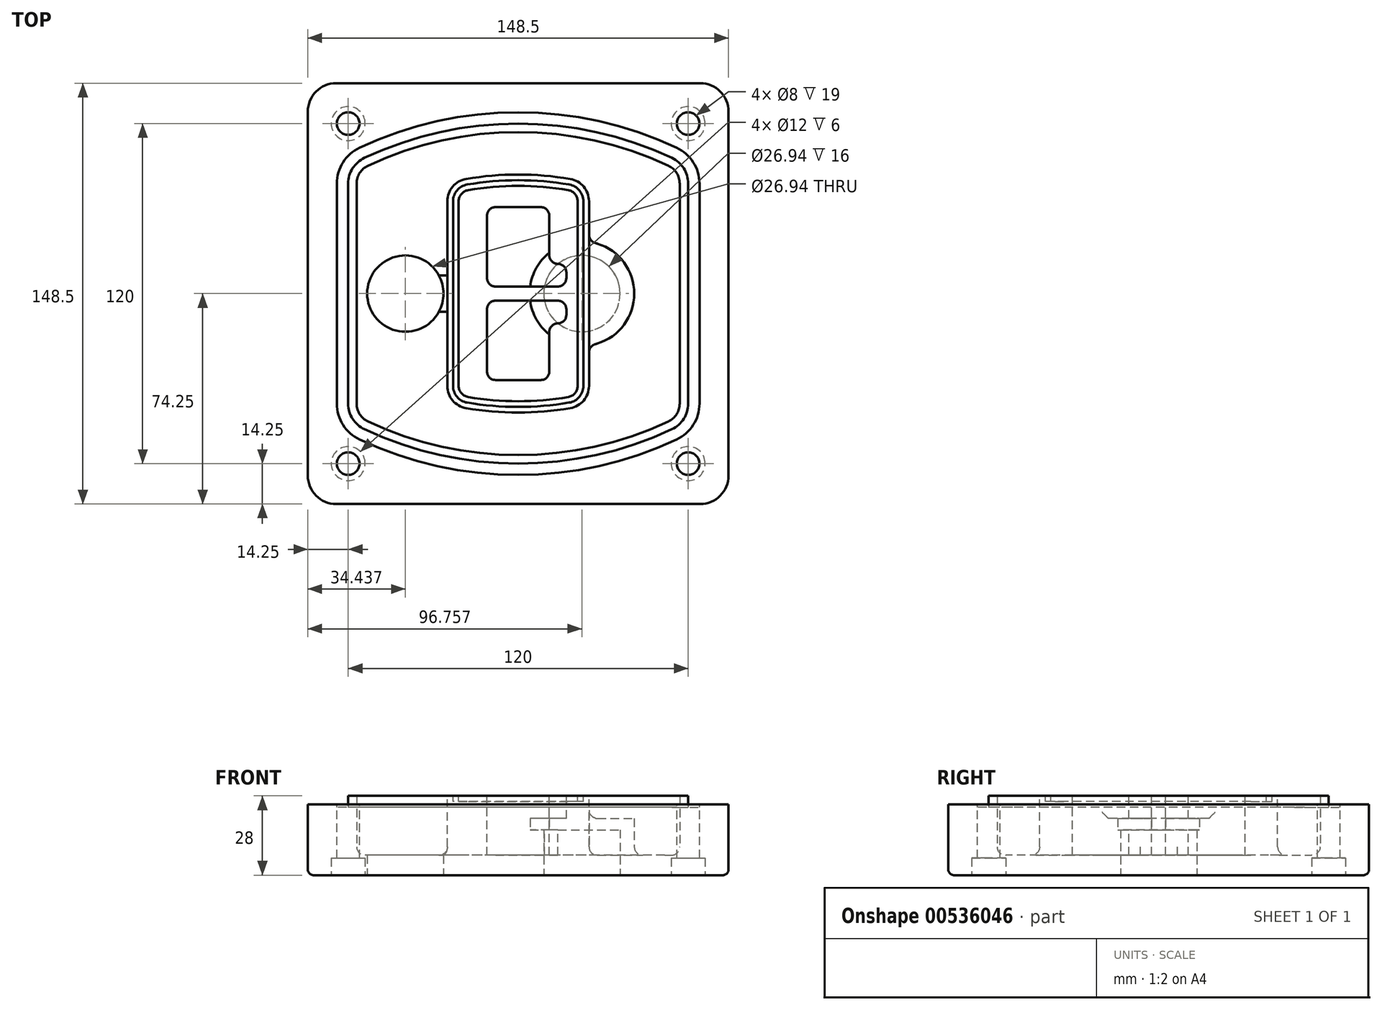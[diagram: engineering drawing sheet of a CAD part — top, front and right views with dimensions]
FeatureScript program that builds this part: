
annotation { "Feature Type Name" : "Feature", "Feature Type Description" : "" }
export const myFeature = defineFeature(function(context is Context, id is Id, definition is map)
    precondition{}
    {
        {
            var Q0;
            Q0=qCreatedBy(makeId("Top.planeOp"),FACE);
            var sketch = newSketch(context, id + "F0", { "sketchPlane" : qUnion([Q0])});
            skPoint(sketch, "E0.rect.middle", {"position": v(0, 0) * mm});
            skLineSegment(sketch, "E1.bottom", {"start": v(-64.25, -74.25) * mm, "end": v(64.25, -74.25) * mm});
            skLineSegment(sketch, "E1.top", {"start": v(-64.25, 74.25) * mm, "end": v(64.25, 74.25) * mm});
            skLineSegment(sketch, "E1.left", {"start": v(-74.25, -64.25) * mm, "end": v(-74.25, 64.25) * mm});
            skLineSegment(sketch, "E1.right", {"start": v(74.25, -64.25) * mm, "end": v(74.25, 64.25) * mm});
            skLineSegment(sketch, "E2", {"start": v(-74.25, 74.25) * mm, "end": v(74.25, -74.25) * mm, "construction": true});
            skLineSegment(sketch, "E3", {"start": v(74.25, 74.25) * mm, "end": v(-74.25, -74.25) * mm, "construction": true});
            skCircle(sketch, "E4", {"center": v(-60, 60) * mm, "radius": 4 * mm});
            skCircle(sketch, "E5", {"center": v(60, 60) * mm, "radius": 4 * mm});
            skCircle(sketch, "E6", {"center": v(60, -60) * mm, "radius": 4 * mm});
            skCircle(sketch, "E7", {"center": v(-60, -60) * mm, "radius": 4 * mm});
            skLineSegment(sketch, "E8", {"start": v(-60, 60) * mm, "end": v(60, 60) * mm, "construction": true});
            skLineSegment(sketch, "E9", {"start": v(60, 60) * mm, "end": v(60, -60) * mm, "construction": true});
            skLineSegment(sketch, "E10", {"start": v(60, -60) * mm, "end": v(-60, -60) * mm, "construction": true});
            skLineSegment(sketch, "E11", {"start": v(-60, -60) * mm, "end": v(-60, 60) * mm, "construction": true});
            skLineSegment(sketch, "E12", {"start": v(-60, 38.83) * mm, "end": v(-60, -38.83) * mm});
            skLineSegment(sketch, "E13", {"start": v(60, 38.83) * mm, "end": v(60, -38.83) * mm});
            skArc(sketch, "E14", {"start": v(54.26, 47.88) * mm, "mid": v(0, 60) * mm, "end": v(-54.26, 47.88) * mm});
            skArc(sketch, "E15", {"start": v(-54.26, -47.88) * mm, "mid": v(0, -60) * mm, "end": v(54.26, -47.88) * mm});
            skLineSegment(sketch, "E16", {"start": v(-60, 0) * mm, "end": v(60, 0) * mm, "construction": true});
            skPoint(sketch, "E17.visualSharp", {"position": v(-60, -45) * mm});
            skArc(sketch, "E17.filletArc", {"start": v(-60, -38.83) * mm, "mid": v(-58.44, -44.2) * mm, "end": v(-54.26, -47.88) * mm});
            skPoint(sketch, "E18.visualSharp", {"position": v(-60, 45) * mm});
            skArc(sketch, "E18.filletArc", {"start": v(-54.26, 47.88) * mm, "mid": v(-58.44, 44.2) * mm, "end": v(-60, 38.83) * mm});
            skPoint(sketch, "E19.visualSharp", {"position": v(60, 45) * mm});
            skArc(sketch, "E19.filletArc", {"start": v(60, 38.83) * mm, "mid": v(58.44, 44.2) * mm, "end": v(54.26, 47.88) * mm});
            skPoint(sketch, "E20.visualSharp", {"position": v(60, -45) * mm});
            skArc(sketch, "E20.filletArc", {"start": v(54.26, -47.88) * mm, "mid": v(58.44, -44.2) * mm, "end": v(60, -38.83) * mm});
            skPoint(sketch, "E21.visualSharp", {"position": v(-74.25, 74.25) * mm});
            skArc(sketch, "E21.filletArc", {"start": v(-64.25, 74.25) * mm, "mid": v(-71.32, 71.32) * mm, "end": v(-74.25, 64.25) * mm});
            skPoint(sketch, "E22.visualSharp", {"position": v(74.25, 74.25) * mm});
            skArc(sketch, "E22.filletArc", {"start": v(74.25, 64.25) * mm, "mid": v(71.32, 71.32) * mm, "end": v(64.25, 74.25) * mm});
            skPoint(sketch, "E23.visualSharp", {"position": v(74.25, -74.25) * mm});
            skArc(sketch, "E23.filletArc", {"start": v(64.25, -74.25) * mm, "mid": v(71.32, -71.32) * mm, "end": v(74.25, -64.25) * mm});
            skPoint(sketch, "E24.visualSharp", {"position": v(-74.25, -74.25) * mm});
            skArc(sketch, "E24.filletArc", {"start": v(-74.25, -64.25) * mm, "mid": v(-71.32, -71.32) * mm, "end": v(-64.25, -74.25) * mm});
            skArc(sketch, "E25.0", {"start": v(57, 38.83) * mm, "mid": v(55.9, 42.58) * mm, "end": v(52.98, 45.17) * mm});
            skLineSegment(sketch, "E25.1", {"start": v(57, 38.83) * mm, "end": v(57, -38.83) * mm});
            skArc(sketch, "E25.2", {"start": v(52.98, -45.17) * mm, "mid": v(55.9, -42.58) * mm, "end": v(57, -38.83) * mm});
            skArc(sketch, "E25.3", {"start": v(-52.98, -45.17) * mm, "mid": v(0, -57) * mm, "end": v(52.98, -45.17) * mm});
            skArc(sketch, "E25.4", {"start": v(-57, -38.83) * mm, "mid": v(-55.9, -42.58) * mm, "end": v(-52.98, -45.17) * mm});
            skArc(sketch, "E25.5", {"start": v(52.98, 45.17) * mm, "mid": v(0, 57) * mm, "end": v(-52.98, 45.17) * mm});
            skLineSegment(sketch, "E25.6", {"start": v(-57, 38.83) * mm, "end": v(-57, -38.83) * mm});
            skArc(sketch, "E25.7", {"start": v(-52.98, 45.17) * mm, "mid": v(-55.9, 42.58) * mm, "end": v(-57, 38.83) * mm});
            skArc(sketch, "E26.0", {"start": v(-55.96, 51.5) * mm, "mid": v(-61.82, 46.33) * mm, "end": v(-64, 38.83) * mm});
            skArc(sketch, "E26.1", {"start": v(55.96, 51.5) * mm, "mid": v(0, 64) * mm, "end": v(-55.96, 51.5) * mm});
            skArc(sketch, "E26.2", {"start": v(64, 38.83) * mm, "mid": v(61.82, 46.33) * mm, "end": v(55.96, 51.5) * mm});
            skLineSegment(sketch, "E26.3", {"start": v(64, 38.83) * mm, "end": v(64, -38.83) * mm});
            skArc(sketch, "E26.4", {"start": v(55.96, -51.5) * mm, "mid": v(61.82, -46.33) * mm, "end": v(64, -38.83) * mm});
            skLineSegment(sketch, "E26.5", {"start": v(-64, 38.83) * mm, "end": v(-64, -38.83) * mm});
            skArc(sketch, "E26.6", {"start": v(-55.96, -51.5) * mm, "mid": v(0, -64) * mm, "end": v(55.96, -51.5) * mm});
            skArc(sketch, "E26.7", {"start": v(-64, -38.83) * mm, "mid": v(-61.82, -46.33) * mm, "end": v(-55.96, -51.5) * mm});
            skSolve(sketch);
        }
        {
            var Q0;
            Q0=makeQuery(id+"F0.imprint","IMPRINT",FACE,{"disambiguationData":[TD([[makeQuery(id+"F0.imprint","IMPRINT",EDGE,{"derivedFrom":sQuery(id+"F0.wireOp",EDGE,"E1.bottom")}),1.0]])]});
            var Q1;
            Q1=makeQuery(id+"F0.imprint","IMPRINT",FACE,{"disambiguationData":[TD([[makeQuery(id+"F0.imprint","IMPRINT",EDGE,{"derivedFrom":sQuery(id+"F0.wireOp",EDGE,"E12")}),1.0]])]});
            var Q2;
            Q2=makeQuery(id+"F0.imprint","IMPRINT",FACE,{"disambiguationData":[TD([[makeQuery(id+"F0.imprint","IMPRINT",EDGE,{"derivedFrom":sQuery(id+"F0.wireOp",EDGE,"E25.0")}),1.0]])]});
            var Q3;
            Q3=makeQuery(id+"F0.imprint","IMPRINT",FACE,{"disambiguationData":[TD([[makeQuery(id+"F0.imprint","IMPRINT",EDGE,{"derivedFrom":sQuery(id+"F0.wireOp",EDGE,"E12")}),-1.0]])]});
            extrude(context, id + "F1", {"entities" : qUnion([Q0, Q1, Q2, Q3]), "oppositeDirection" : true, "depth" : 25 * mm, "offsetDistance" : 25 * mm});
        }
        {
            var Q0;
            Q0=makeQuery(id+"F0.imprint","IMPRINT",FACE,{"disambiguationData":[TD([[makeQuery(id+"F0.imprint","IMPRINT",EDGE,{"derivedFrom":sQuery(id+"F0.wireOp",EDGE,"E12")}),1.0]])]});
            extrude(context, id + "F2", {"entities" : qUnion([Q0]), "operationType" : NewBodyOperationType.ADD, "depth" : 3 * mm, "offsetDistance" : 25 * mm});
        }
        {
            var Q0;
            Q0=makeQuery(id+"F0.imprint","IMPRINT",FACE,{"disambiguationData":[TD([[makeQuery(id+"F0.imprint","IMPRINT",EDGE,{"derivedFrom":sQuery(id+"F0.wireOp",EDGE,"E12")}),-1.0]])]});
            extrude(context, id + "F3", {"entities" : qUnion([Q0]), "operationType" : NewBodyOperationType.REMOVE, "oppositeDirection" : true, "depth" : 1 * mm});
        }
        {
            var Q0;
            Q0=makeQuery(id+"F0.imprint","IMPRINT",FACE,{"disambiguationData":[TD([[makeQuery(id+"F0.imprint","IMPRINT",EDGE,{"derivedFrom":sQuery(id+"F0.wireOp",EDGE,"E25.0")}),1.0]])]});
            extrude(context, id + "F4", {"entities" : qUnion([Q0]), "operationType" : NewBodyOperationType.REMOVE, "oppositeDirection" : true, "depth" : 18 * mm});
        }
        {
            var Q0;
            Q0=makeQuery(id+"F2.opExtrude","CAP_FACE",FACE,{"disambiguationData":[OSD([sQuery(id+"F0.wireOp",EDGE,"E12"),sQuery(id+"F0.wireOp",EDGE,"E13"),sQuery(id+"F0.wireOp",EDGE,"E14"),sQuery(id+"F0.wireOp",EDGE,"E15"),sQuery(id+"F0.wireOp",EDGE,"E17.filletArc"),sQuery(id+"F0.wireOp",EDGE,"E18.filletArc"),sQuery(id+"F0.wireOp",EDGE,"E19.filletArc"),sQuery(id+"F0.wireOp",EDGE,"E20.filletArc"),sQuery(id+"F0.wireOp",EDGE,"E25.0"),sQuery(id+"F0.wireOp",EDGE,"E25.1"),sQuery(id+"F0.wireOp",EDGE,"E25.2"),sQuery(id+"F0.wireOp",EDGE,"E25.3"),sQuery(id+"F0.wireOp",EDGE,"E25.4"),sQuery(id+"F0.wireOp",EDGE,"E25.5"),sQuery(id+"F0.wireOp",EDGE,"E25.6"),sQuery(id+"F0.wireOp",EDGE,"E25.7")])],"isStart":false});
            var sketch = newSketch(context, id + "F5", { "sketchPlane" : qUnion([Q0])});
            skArc(sketch, "E27.0", {"start": v(-18.34, -40.45) * mm, "mid": v(0, -42) * mm, "end": v(18.34, -40.45) * mm});
            skArc(sketch, "E28.0", {"start": v(18.34, 40.45) * mm, "mid": v(0, 42) * mm, "end": v(-18.34, 40.45) * mm});
            skLineSegment(sketch, "E29", {"start": v(-25, 32.57) * mm, "end": v(-25, -32.57) * mm});
            skLineSegment(sketch, "E30", {"start": v(25, 32.57) * mm, "end": v(25, -32.57) * mm});
            skLineSegment(sketch, "E31", {"start": v(-25, 39.1) * mm, "end": v(25, 39.1) * mm, "construction": true});
            skLineSegment(sketch, "E32", {"start": v(-25, -39.1) * mm, "end": v(25, -39.1) * mm, "construction": true});
            skPoint(sketch, "E33.visualSharp", {"position": v(-25, 39.1) * mm});
            skArc(sketch, "E33.filletArc", {"start": v(-18.34, 40.45) * mm, "mid": v(-23.11, 37.73) * mm, "end": v(-25, 32.57) * mm});
            skPoint(sketch, "E34.visualSharp", {"position": v(25, 39.1) * mm});
            skArc(sketch, "E34.filletArc", {"start": v(25, 32.57) * mm, "mid": v(23.11, 37.73) * mm, "end": v(18.34, 40.45) * mm});
            skPoint(sketch, "E35.visualSharp", {"position": v(25, -39.1) * mm});
            skArc(sketch, "E35.filletArc", {"start": v(18.34, -40.45) * mm, "mid": v(23.11, -37.73) * mm, "end": v(25, -32.57) * mm});
            skPoint(sketch, "E36.visualSharp", {"position": v(-25, -39.1) * mm});
            skArc(sketch, "E36.filletArc", {"start": v(-25, -32.57) * mm, "mid": v(-23.11, -37.73) * mm, "end": v(-18.34, -40.45) * mm});
            skArc(sketch, "E37.0", {"start": v(52.98, 45.17) * mm, "mid": v(0, 57) * mm, "end": v(-52.98, 45.17) * mm});
            skArc(sketch, "E37.1", {"start": v(-52.98, 45.17) * mm, "mid": v(-55.9, 42.58) * mm, "end": v(-57, 38.83) * mm});
            skLineSegment(sketch, "E37.2", {"start": v(-57, 38.83) * mm, "end": v(-57, -38.83) * mm});
            skArc(sketch, "E37.3", {"start": v(-57, -38.83) * mm, "mid": v(-55.9, -42.58) * mm, "end": v(-52.98, -45.17) * mm});
            skArc(sketch, "E37.4", {"start": v(-52.98, -45.17) * mm, "mid": v(0, -57) * mm, "end": v(52.98, -45.17) * mm});
            skArc(sketch, "E37.5", {"start": v(52.98, -45.17) * mm, "mid": v(55.9, -42.58) * mm, "end": v(57, -38.83) * mm});
            skLineSegment(sketch, "E37.6", {"start": v(57, 38.83) * mm, "end": v(57, -38.83) * mm});
            skArc(sketch, "E37.7", {"start": v(57, 38.83) * mm, "mid": v(55.9, 42.58) * mm, "end": v(52.98, 45.17) * mm});
            skLineSegment(sketch, "E38.0", {"start": v(23, 32.57) * mm, "end": v(23, -32.57) * mm});
            skArc(sketch, "E38.1", {"start": v(18, -38.48) * mm, "mid": v(21.58, -36.44) * mm, "end": v(23, -32.57) * mm});
            skArc(sketch, "E38.2", {"start": v(-18, -38.48) * mm, "mid": v(0, -40) * mm, "end": v(18, -38.48) * mm});
            skArc(sketch, "E38.3", {"start": v(-23, -32.57) * mm, "mid": v(-21.58, -36.44) * mm, "end": v(-18, -38.48) * mm});
            skLineSegment(sketch, "E38.4", {"start": v(-23, 32.57) * mm, "end": v(-23, -32.57) * mm});
            skArc(sketch, "E38.5", {"start": v(23, 32.57) * mm, "mid": v(21.58, 36.44) * mm, "end": v(18, 38.48) * mm});
            skArc(sketch, "E38.6", {"start": v(-18, 38.48) * mm, "mid": v(-21.58, 36.44) * mm, "end": v(-23, 32.57) * mm});
            skArc(sketch, "E38.7", {"start": v(18, 38.48) * mm, "mid": v(0, 40) * mm, "end": v(-18, 38.48) * mm});
            skArc(sketch, "E39.0", {"start": v(21, 32.57) * mm, "mid": v(20.06, 35.15) * mm, "end": v(17.67, 36.5) * mm});
            skLineSegment(sketch, "E39.1", {"start": v(21, 32.57) * mm, "end": v(21, -32.57) * mm});
            skArc(sketch, "E39.2", {"start": v(17.67, -36.5) * mm, "mid": v(20.06, -35.15) * mm, "end": v(21, -32.57) * mm});
            skArc(sketch, "E39.3", {"start": v(-17.67, -36.5) * mm, "mid": v(0, -38) * mm, "end": v(17.67, -36.5) * mm});
            skArc(sketch, "E39.4", {"start": v(-21, -32.57) * mm, "mid": v(-20.06, -35.15) * mm, "end": v(-17.67, -36.5) * mm});
            skArc(sketch, "E39.5", {"start": v(17.67, 36.5) * mm, "mid": v(0, 38) * mm, "end": v(-17.67, 36.5) * mm});
            skLineSegment(sketch, "E39.6", {"start": v(-21, 32.57) * mm, "end": v(-21, -32.57) * mm});
            skArc(sketch, "E39.7", {"start": v(-17.67, 36.5) * mm, "mid": v(-20.06, 35.15) * mm, "end": v(-21, 32.57) * mm});
            skLineSegment(sketch, "E40", {"start": v(-25, 0) * mm, "end": v(25, 0) * mm, "construction": true});
            skLineSegment(sketch, "E41", {"start": v(-11, 5.5) * mm, "end": v(-11, 27.5) * mm});
            skLineSegment(sketch, "E42", {"start": v(-8, 30.5) * mm, "end": v(8, 30.5) * mm});
            skLineSegment(sketch, "E43", {"start": v(11, 27.5) * mm, "end": v(11, 13.5) * mm});
            skLineSegment(sketch, "E44", {"start": v(14, 10.5) * mm, "end": v(14, 10.5) * mm});
            skLineSegment(sketch, "E45", {"start": v(17, 7.5) * mm, "end": v(17, 5.5) * mm});
            skLineSegment(sketch, "E46", {"start": v(14, 2.5) * mm, "end": v(-8, 2.5) * mm});
            skPoint(sketch, "E47.visualSharp", {"position": v(-11, 30.5) * mm});
            skArc(sketch, "E47.filletArc", {"start": v(-8, 30.5) * mm, "mid": v(-10.12, 29.62) * mm, "end": v(-11, 27.5) * mm});
            skPoint(sketch, "E48.visualSharp", {"position": v(11, 30.5) * mm});
            skArc(sketch, "E48.filletArc", {"start": v(11, 27.5) * mm, "mid": v(10.12, 29.62) * mm, "end": v(8, 30.5) * mm});
            skPoint(sketch, "E49.visualSharp", {"position": v(11, 10.5) * mm});
            skArc(sketch, "E49.filletArc", {"start": v(11, 13.5) * mm, "mid": v(11.88, 11.38) * mm, "end": v(14, 10.5) * mm});
            skPoint(sketch, "E50.visualSharp", {"position": v(17, 10.5) * mm});
            skArc(sketch, "E50.filletArc", {"start": v(17, 7.5) * mm, "mid": v(16.12, 9.62) * mm, "end": v(14, 10.5) * mm});
            skPoint(sketch, "E51.visualSharp", {"position": v(17, 2.5) * mm});
            skArc(sketch, "E51.filletArc", {"start": v(14, 2.5) * mm, "mid": v(16.12, 3.38) * mm, "end": v(17, 5.5) * mm});
            skPoint(sketch, "E52.visualSharp", {"position": v(-11, 2.5) * mm});
            skArc(sketch, "E52.filletArc", {"start": v(-11, 5.5) * mm, "mid": v(-10.12, 3.38) * mm, "end": v(-8, 2.5) * mm});
            skLineSegment(sketch, "E53.0.MirrorCS", {"start": v(14, -2.5) * mm, "end": v(-8, -2.5) * mm});
            skArc(sketch, "E54.0.MirrorCS", {"start": v(-11, -5.5) * mm, "mid": v(-10.12, -3.38) * mm, "end": v(-8, -2.5) * mm});
            skLineSegment(sketch, "E55.0.MirrorCS", {"start": v(-11, -5.5) * mm, "end": v(-11, -27.5) * mm});
            skArc(sketch, "E56.0.MirrorCS", {"start": v(-8, -30.5) * mm, "mid": v(-10.12, -29.62) * mm, "end": v(-11, -27.5) * mm});
            skLineSegment(sketch, "E57.0.MirrorCS", {"start": v(-8, -30.5) * mm, "end": v(8, -30.5) * mm});
            skArc(sketch, "E58.0.MirrorCS", {"start": v(11, -27.5) * mm, "mid": v(10.12, -29.62) * mm, "end": v(8, -30.5) * mm});
            skLineSegment(sketch, "E59.0.MirrorCS", {"start": v(11, -27.5) * mm, "end": v(11, -13.5) * mm});
            skArc(sketch, "E60.0.MirrorCS", {"start": v(11, -13.5) * mm, "mid": v(11.88, -11.38) * mm, "end": v(14, -10.5) * mm});
            skArc(sketch, "E61.0.MirrorCS", {"start": v(17, -7.5) * mm, "mid": v(16.12, -9.62) * mm, "end": v(14, -10.5) * mm});
            skLineSegment(sketch, "E62.0.MirrorCS", {"start": v(17, -7.5) * mm, "end": v(17, -5.5) * mm});
            skArc(sketch, "E63.0.MirrorCS", {"start": v(14, -2.5) * mm, "mid": v(16.12, -3.38) * mm, "end": v(17, -5.5) * mm});
            skSolve(sketch);
        }
        {
            var Q0;
            Q0=makeQuery(id+"F5.imprint","IMPRINT",FACE,{"disambiguationData":[TD([[makeQuery(id+"F5.imprint","IMPRINT",EDGE,{"derivedFrom":sQuery(id+"F5.wireOp",EDGE,"E27.0")}),1.0]])]});
            var Q1;
            Q1=makeQuery(id+"F5.imprint","IMPRINT",FACE,{"disambiguationData":[TD([[makeQuery(id+"F5.imprint","IMPRINT",EDGE,{"derivedFrom":sQuery(id+"F5.wireOp",EDGE,"E38.0")}),-1.0]])]});
            var Q2;
            Q2=makeQuery(id+"F5.imprint","IMPRINT",FACE,{"disambiguationData":[TD([[makeQuery(id+"F5.imprint","IMPRINT",EDGE,{"derivedFrom":sQuery(id+"F5.wireOp",EDGE,"E39.0")}),1.0]])]});
            extrude(context, id + "F6", {"entities" : qUnion([Q0, Q1, Q2]), "operationType" : NewBodyOperationType.ADD, "endBound" : BoundingType.UP_TO_NEXT, "oppositeDirection" : true, "depth" : 25 * mm});
        }
        {
            var Q0;
            Q0=makeQuery(id+"F5.imprint","IMPRINT",FACE,{"disambiguationData":[TD([[makeQuery(id+"F5.imprint","IMPRINT",EDGE,{"derivedFrom":sQuery(id+"F5.wireOp",EDGE,"E38.0")}),-1.0]])]});
            extrude(context, id + "F7", {"entities" : qUnion([Q0]), "operationType" : NewBodyOperationType.REMOVE, "oppositeDirection" : true, "depth" : 2 * mm});
        }
        {
            var Q0;
            Q0=makeQuery(id+"F1.opExtrude","CAP_FACE",FACE,{"disambiguationData":[OSD([sQuery(id+"F0.wireOp",EDGE,"E1.bottom"),sQuery(id+"F0.wireOp",EDGE,"E1.top"),sQuery(id+"F0.wireOp",EDGE,"E1.left"),sQuery(id+"F0.wireOp",EDGE,"E1.right"),sQuery(id+"F0.wireOp",EDGE,"E4"),sQuery(id+"F0.wireOp",EDGE,"E5"),sQuery(id+"F0.wireOp",EDGE,"E6"),sQuery(id+"F0.wireOp",EDGE,"E7"),sQuery(id+"F0.wireOp",EDGE,"E21.filletArc"),sQuery(id+"F0.wireOp",EDGE,"E22.filletArc"),sQuery(id+"F0.wireOp",EDGE,"E23.filletArc"),sQuery(id+"F0.wireOp",EDGE,"E24.filletArc")])],"isStart":false});
            var sketch = newSketch(context, id + "F8", { "sketchPlane" : qUnion([Q0])});
            skCircle(sketch, "E64", {"center": v(22.5, 0) * mm, "radius": 13.47 * mm});
            skCircle(sketch, "E65", {"center": v(-39.81, 0) * mm, "radius": 13.47 * mm});
            skLineSegment(sketch, "E66", {"start": v(74.25, 0) * mm, "end": v(-74.25, 0) * mm});
            skCircle(sketch, "E67", {"center": v(22.5, 0) * mm, "radius": 18.47 * mm});
            skCircle(sketch, "E68", {"center": v(60, -60) * mm, "radius": 6 * mm});
            skCircle(sketch, "E69", {"center": v(-60, -60) * mm, "radius": 6 * mm});
            skCircle(sketch, "E70", {"center": v(-60, 60) * mm, "radius": 6 * mm});
            skCircle(sketch, "E71", {"center": v(60, 60) * mm, "radius": 6 * mm});
            skSolve(sketch);
        }
        {
            var Q0;
            {var subQ1=sQuery(id+"F8.wireOp",EDGE,"E66");var subQ4=sQuery(id+"F8.wireOp",EDGE,"E64");var subQ6=makeQuery(id+"F8.imprint","INTERSECT",VERTEX,{"disambiguationData":[OD(0.0)],"derivedFrom":[subQ4,subQ1]});Q0=makeQuery(id+"F8.imprint","IMPRINT",FACE,{"disambiguationData":[TD([[makeQuery(id+"F8.imprint","IMPRINT",EDGE,{"disambiguationData":[TD([[subQ6,-1.0]])],"derivedFrom":subQ4}),-1.0]])]});}
            var Q1;
            {var subQ0=sQuery(id+"F8.wireOp",EDGE,"E66");var subQ1=sQuery(id+"F8.wireOp",EDGE,"E64");var subQ3=makeQuery(id+"F8.imprint","INTERSECT",VERTEX,{"disambiguationData":[OD(0.0)],"derivedFrom":[subQ1,subQ0]});Q1=makeQuery(id+"F8.imprint","IMPRINT",FACE,{"disambiguationData":[TD([[makeQuery(id+"F8.imprint","IMPRINT",EDGE,{"disambiguationData":[TD([[subQ3,-1.0]])],"derivedFrom":subQ1}),1.0]])]});}
            var Q2;
            {var subQ0=sQuery(id+"F8.wireOp",EDGE,"E66");var subQ1=sQuery(id+"F8.wireOp",EDGE,"E64");var subQ3=makeQuery(id+"F8.imprint","INTERSECT",VERTEX,{"disambiguationData":[OD(0.0)],"derivedFrom":[subQ1,subQ0]});Q2=makeQuery(id+"F8.imprint","IMPRINT",FACE,{"disambiguationData":[TD([[makeQuery(id+"F8.imprint","IMPRINT",EDGE,{"disambiguationData":[TD([[subQ3,1.0]])],"derivedFrom":subQ1}),1.0]])]});}
            var Q3;
            {var subQ1=sQuery(id+"F8.wireOp",EDGE,"E66");var subQ4=sQuery(id+"F8.wireOp",EDGE,"E64");var subQ6=makeQuery(id+"F8.imprint","INTERSECT",VERTEX,{"disambiguationData":[OD(0.0)],"derivedFrom":[subQ4,subQ1]});Q3=makeQuery(id+"F8.imprint","IMPRINT",FACE,{"disambiguationData":[TD([[makeQuery(id+"F8.imprint","IMPRINT",EDGE,{"disambiguationData":[TD([[subQ6,1.0]])],"derivedFrom":subQ4}),-1.0]])]});}
            extrude(context, id + "F9", {"entities" : qUnion([Q0, Q1, Q2, Q3]), "operationType" : NewBodyOperationType.ADD, "oppositeDirection" : true, "depth" : 20 * mm});
        }
        {
            var Q0;
            {var subQ0=sQuery(id+"F8.wireOp",EDGE,"E66");var subQ1=sQuery(id+"F8.wireOp",EDGE,"E64");var subQ3=makeQuery(id+"F8.imprint","INTERSECT",VERTEX,{"disambiguationData":[OD(0.0)],"derivedFrom":[subQ1,subQ0]});Q0=makeQuery(id+"F8.imprint","IMPRINT",FACE,{"disambiguationData":[TD([[makeQuery(id+"F8.imprint","IMPRINT",EDGE,{"disambiguationData":[TD([[subQ3,-1.0]])],"derivedFrom":subQ1}),1.0]])]});}
            var Q1;
            {var subQ0=sQuery(id+"F8.wireOp",EDGE,"E66");var subQ1=sQuery(id+"F8.wireOp",EDGE,"E64");var subQ3=makeQuery(id+"F8.imprint","INTERSECT",VERTEX,{"disambiguationData":[OD(0.0)],"derivedFrom":[subQ1,subQ0]});Q1=makeQuery(id+"F8.imprint","IMPRINT",FACE,{"disambiguationData":[TD([[makeQuery(id+"F8.imprint","IMPRINT",EDGE,{"disambiguationData":[TD([[subQ3,1.0]])],"derivedFrom":subQ1}),1.0]])]});}
            extrude(context, id + "F10", {"entities" : qUnion([Q0, Q1]), "operationType" : NewBodyOperationType.REMOVE, "oppositeDirection" : true, "depth" : 16 * mm});
        }
        {
            var Q0;
            {var subQ0=sQuery(id+"F8.wireOp",EDGE,"E66");var subQ1=sQuery(id+"F8.wireOp",EDGE,"E65");var subQ3=makeQuery(id+"F8.imprint","INTERSECT",VERTEX,{"disambiguationData":[OD(0.0)],"derivedFrom":[subQ1,subQ0]});Q0=makeQuery(id+"F8.imprint","IMPRINT",FACE,{"disambiguationData":[TD([[makeQuery(id+"F8.imprint","IMPRINT",EDGE,{"disambiguationData":[TD([[subQ3,-1.0]])],"derivedFrom":subQ1}),1.0]])]});}
            var Q1;
            {var subQ0=sQuery(id+"F8.wireOp",EDGE,"E66");var subQ1=sQuery(id+"F8.wireOp",EDGE,"E65");var subQ3=makeQuery(id+"F8.imprint","INTERSECT",VERTEX,{"disambiguationData":[OD(0.0)],"derivedFrom":[subQ1,subQ0]});Q1=makeQuery(id+"F8.imprint","IMPRINT",FACE,{"disambiguationData":[TD([[makeQuery(id+"F8.imprint","IMPRINT",EDGE,{"disambiguationData":[TD([[subQ3,1.0]])],"derivedFrom":subQ1}),1.0]])]});}
            extrude(context, id + "F11", {"entities" : qUnion([Q0, Q1]), "operationType" : NewBodyOperationType.REMOVE, "oppositeDirection" : true, "depth" : 25 * mm});
        }
        {
            var Q0;
            Q0=makeQuery(id+"F8.imprint","IMPRINT",FACE,{"disambiguationData":[TD([[makeQuery(id+"F8.imprint","IMPRINT",EDGE,{"derivedFrom":sQuery(id+"F8.wireOp",EDGE,"E68")}),1.0]])]});
            var Q1;
            Q1=makeQuery(id+"F8.imprint","IMPRINT",FACE,{"disambiguationData":[TD([[makeQuery(id+"F8.imprint","IMPRINT",EDGE,{"derivedFrom":makeQuery(id+"F1.opExtrude","CAP_EDGE",EDGE,{"disambiguationData":[OSD([sQuery(id+"F0.wireOp",EDGE,"E5")])],"isStart":false})}),-1.0]])]});
            var Q2;
            Q2=makeQuery(id+"F8.imprint","IMPRINT",FACE,{"disambiguationData":[TD([[makeQuery(id+"F8.imprint","IMPRINT",EDGE,{"derivedFrom":sQuery(id+"F8.wireOp",EDGE,"E69")}),1.0]])]});
            var Q3;
            Q3=makeQuery(id+"F8.imprint","IMPRINT",FACE,{"disambiguationData":[TD([[makeQuery(id+"F8.imprint","IMPRINT",EDGE,{"derivedFrom":makeQuery(id+"F1.opExtrude","CAP_EDGE",EDGE,{"disambiguationData":[OSD([sQuery(id+"F0.wireOp",EDGE,"E4")])],"isStart":false})}),-1.0]])]});
            var Q4;
            Q4=makeQuery(id+"F8.imprint","IMPRINT",FACE,{"disambiguationData":[TD([[makeQuery(id+"F8.imprint","IMPRINT",EDGE,{"derivedFrom":sQuery(id+"F8.wireOp",EDGE,"E70")}),1.0]])]});
            var Q5;
            Q5=makeQuery(id+"F8.imprint","IMPRINT",FACE,{"disambiguationData":[TD([[makeQuery(id+"F8.imprint","IMPRINT",EDGE,{"derivedFrom":makeQuery(id+"F1.opExtrude","CAP_EDGE",EDGE,{"disambiguationData":[OSD([sQuery(id+"F0.wireOp",EDGE,"E7")])],"isStart":false})}),-1.0]])]});
            var Q6;
            Q6=makeQuery(id+"F8.imprint","IMPRINT",FACE,{"disambiguationData":[TD([[makeQuery(id+"F8.imprint","IMPRINT",EDGE,{"derivedFrom":sQuery(id+"F8.wireOp",EDGE,"E71")}),1.0]])]});
            var Q7;
            Q7=makeQuery(id+"F8.imprint","IMPRINT",FACE,{"disambiguationData":[TD([[makeQuery(id+"F8.imprint","IMPRINT",EDGE,{"derivedFrom":makeQuery(id+"F1.opExtrude","CAP_EDGE",EDGE,{"disambiguationData":[OSD([sQuery(id+"F0.wireOp",EDGE,"E6")])],"isStart":false})}),-1.0]])]});
            extrude(context, id + "F12", {"entities" : qUnion([Q0, Q1, Q2, Q3, Q4, Q5, Q6, Q7]), "operationType" : NewBodyOperationType.REMOVE, "oppositeDirection" : true, "depth" : 6 * mm});
        }
        {
            var Q0;
            Q0=makeQuery(id+"F10.boolean.opBoolean","COPY",FACE,{"derivedFrom":makeQuery(id+"F10.opExtrude","CAP_FACE",FACE,{"disambiguationData":[OSD([sQuery(id+"F8.wireOp",EDGE,"E64")])],"isStart":false})});
            var sketch = newSketch(context, id + "F13", { "sketchPlane" : qUnion([Q0])});
            skArc(sketch, "E72.0", {"start": v(11, 14.45) * mm, "mid": v(6.45, 9.13) * mm, "end": v(4.2, 2.5) * mm});
            skArc(sketch, "E72.1", {"start": v(4.2, -2.5) * mm, "mid": v(6.45, -9.13) * mm, "end": v(11, -14.45) * mm});
            skLineSegment(sketch, "E73", {"start": v(4.2, -2.5) * mm, "end": v(14, -2.5) * mm});
            skLineSegment(sketch, "E74.0", {"start": v(14, 2.5) * mm, "end": v(4.2, 2.5) * mm});
            skArc(sketch, "E74.1", {"start": v(14, 2.5) * mm, "mid": v(16.12, 3.38) * mm, "end": v(17, 5.5) * mm});
            skLineSegment(sketch, "E74.2", {"start": v(17, 7.5) * mm, "end": v(17, 5.5) * mm});
            skArc(sketch, "E74.3", {"start": v(17, 7.5) * mm, "mid": v(16.12, 9.62) * mm, "end": v(14, 10.5) * mm});
            skArc(sketch, "E74.4", {"start": v(11, 13.5) * mm, "mid": v(11.88, 11.38) * mm, "end": v(14, 10.5) * mm});
            skLineSegment(sketch, "E74.5", {"start": v(11, 14.45) * mm, "end": v(11, 13.5) * mm});
            skLineSegment(sketch, "E74.7", {"start": v(14, -2.5) * mm, "end": v(4.2, -2.5) * mm});
            skArc(sketch, "E74.8", {"start": v(14, -2.5) * mm, "mid": v(16.12, -3.38) * mm, "end": v(17, -5.5) * mm});
            skLineSegment(sketch, "E74.9", {"start": v(17, -7.5) * mm, "end": v(17, -5.5) * mm});
            skArc(sketch, "E74.10", {"start": v(17, -7.5) * mm, "mid": v(16.12, -9.62) * mm, "end": v(14, -10.5) * mm});
            skArc(sketch, "E74.11", {"start": v(11, -13.5) * mm, "mid": v(11.88, -11.38) * mm, "end": v(14, -10.5) * mm});
            skLineSegment(sketch, "E74.12", {"start": v(11, -14.45) * mm, "end": v(11, -13.5) * mm});
            skPoint(sketch, "E75.orphan", {"position": v(11, -27.5) * mm});
            skPoint(sketch, "E76.orphan", {"position": v(-8, -2.5) * mm});
            skPoint(sketch, "E77.orphan", {"position": v(-8, 2.5) * mm});
            skPoint(sketch, "E78.orphan", {"position": v(11, 27.5) * mm});
            skSolve(sketch);
        }
        {
            var Q0;
            {var subQ7=sQuery(id+"F13.wireOp",EDGE,"E72.0");var subQ14=sQuery(id+"F13.wireOp",EDGE,"E72.1");var subQ16=sQuery(id+"F13.wireOp",EDGE,"E74.1");var subQ18=sQuery(id+"F13.wireOp",EDGE,"E74.8");Q0=qUnion([makeQuery(id+"F13.imprint","IMPRINT",FACE,{"disambiguationData":[TD([[makeQuery(id+"F13.imprint","IMPRINT",EDGE,{"derivedFrom":subQ7}),1.0]])]}),makeQuery(id+"F13.imprint","IMPRINT",FACE,{"disambiguationData":[TD([[makeQuery(id+"F13.imprint","IMPRINT",EDGE,{"derivedFrom":subQ14}),1.0]])]}),makeQuery(id+"F13.imprint","IMPRINT",FACE,{"disambiguationData":[TD([[makeQuery(id+"F13.imprint","IMPRINT",EDGE,{"derivedFrom":subQ16}),1.0]])]}),makeQuery(id+"F13.imprint","IMPRINT",FACE,{"disambiguationData":[TD([[makeQuery(id+"F13.imprint","IMPRINT",EDGE,{"derivedFrom":subQ18}),-1.0]])]})]);}
            var Q1;
            Q1=makeQuery(id+"F6.boolean.opBoolean","SPLIT",FACE,{"disambiguationData":[TD([makeQuery(id+"F6.opExtrude","SWEPT_FACE",FACE,{"disambiguationData":[OSD([sQuery(id+"F5.wireOp",EDGE,"E41")])]})])],"derivedFrom":makeQuery(id+"F4.boolean.opBoolean","COPY",FACE,{"derivedFrom":makeQuery(id+"F4.opExtrude","CAP_FACE",FACE,{"disambiguationData":[OSD([sQuery(id+"F0.wireOp",EDGE,"E25.0"),sQuery(id+"F0.wireOp",EDGE,"E25.1"),sQuery(id+"F0.wireOp",EDGE,"E25.2"),sQuery(id+"F0.wireOp",EDGE,"E25.3"),sQuery(id+"F0.wireOp",EDGE,"E25.4"),sQuery(id+"F0.wireOp",EDGE,"E25.5"),sQuery(id+"F0.wireOp",EDGE,"E25.6"),sQuery(id+"F0.wireOp",EDGE,"E25.7")])],"isStart":false})})});
            extrude(context, id + "F14", {"entities" : qUnion([Q0]), "operationType" : NewBodyOperationType.REMOVE, "endBound" : BoundingType.UP_TO_SURFACE, "endBoundEntityFace" : qUnion([Q1]), "depth" : 25 * mm});
        }
        {
            var Q0;
            Q0=makeQuery(id+"F4.boolean.opBoolean","COPY",EDGE,{"derivedFrom":makeQuery(id+"F4.opExtrude","CAP_EDGE",EDGE,{"disambiguationData":[OSD([sQuery(id+"F0.wireOp",EDGE,"E25.6")])],"isStart":false})});
            var Q1;
            Q1=makeQuery(id+"F9.boolean.opBoolean","INTERSECT",EDGE,{"derivedFrom":[makeQuery(id+"F6.opExtrude","SWEPT_FACE",FACE,{"disambiguationData":[OSD([sQuery(id+"F5.wireOp",EDGE,"E30")])]}),makeQuery(id+"F9.opExtrude","CAP_FACE",FACE,{"disambiguationData":[OSD([sQuery(id+"F8.wireOp",EDGE,"E67")])],"isStart":false})]});
            var Q2;
            Q2=makeQuery(id+"F9.boolean.opBoolean","INTERSECT",EDGE,{"disambiguationData":[OD(1.0)],"derivedFrom":[makeQuery(id+"F6.opExtrude","SWEPT_FACE",FACE,{"disambiguationData":[OSD([sQuery(id+"F5.wireOp",EDGE,"E30")])]}),makeQuery(id+"F9.opExtrude","SWEPT_FACE",FACE,{"disambiguationData":[OSD([sQuery(id+"F8.wireOp",EDGE,"E67")])]})]});
            var Q3;
            {var subQ0=sQuery(id+"F5.wireOp",EDGE,"E30");Q3=makeQuery(id+"F9.boolean.opBoolean","SPLIT",EDGE,{"disambiguationData":[TD([makeQuery(id+"F6.opExtrude","SWEPT_FACE",FACE,{"disambiguationData":[OSD([sQuery(id+"F5.wireOp",EDGE,"E35.filletArc")])]})])],"derivedFrom":makeQuery(id+"F6.opExtrude","CAP_EDGE",EDGE,{"disambiguationData":[OSD([subQ0])],"isStart":false})});}
            var Q4;
            {var subQ0=sQuery(id+"F0.wireOp",EDGE,"E25.7");var subQ1=sQuery(id+"F0.wireOp",EDGE,"E25.6");var subQ2=sQuery(id+"F0.wireOp",EDGE,"E25.5");var subQ3=sQuery(id+"F0.wireOp",EDGE,"E25.4");var subQ4=sQuery(id+"F0.wireOp",EDGE,"E25.0");var subQ5=sQuery(id+"F0.wireOp",EDGE,"E25.1");var subQ6=sQuery(id+"F0.wireOp",EDGE,"E25.2");var subQ7=sQuery(id+"F0.wireOp",EDGE,"E25.3");Q4=makeQuery(id+"F9.boolean.opBoolean","INTERSECT",EDGE,{"derivedFrom":[makeQuery(id+"F6.boolean.opBoolean","SPLIT",FACE,{"disambiguationData":[TD([makeQuery(id+"F2.opExtrude","SWEPT_FACE",FACE,{"disambiguationData":[OSD([subQ4])]})])],"derivedFrom":makeQuery(id+"F4.boolean.opBoolean","COPY",FACE,{"derivedFrom":makeQuery(id+"F4.opExtrude","CAP_FACE",FACE,{"disambiguationData":[OSD([subQ4,subQ5,subQ6,subQ7,subQ3,subQ2,subQ1,subQ0])],"isStart":false})})}),makeQuery(id+"F9.opExtrude","SWEPT_FACE",FACE,{"disambiguationData":[OSD([sQuery(id+"F8.wireOp",EDGE,"E67")])]})]});}
            var Q5;
            Q5=makeQuery(id+"F9.boolean.opBoolean","INTERSECT",EDGE,{"disambiguationData":[OD(0.0)],"derivedFrom":[makeQuery(id+"F6.opExtrude","SWEPT_FACE",FACE,{"disambiguationData":[OSD([sQuery(id+"F5.wireOp",EDGE,"E30")])]}),makeQuery(id+"F9.opExtrude","SWEPT_FACE",FACE,{"disambiguationData":[OSD([sQuery(id+"F8.wireOp",EDGE,"E67")])]})]});
            fillet(context, id + "F15", {"entities" : qUnion([Q0, Q1, Q2, Q3, Q4, Q5]), "radius" : 3 * mm, "tangentPropagation" : true, "allowEdgeOverflow" : false});
        }
        {
            var Q0;
            Q0=makeQuery(id+"F1.opExtrude","CAP_EDGE",EDGE,{"disambiguationData":[OSD([sQuery(id+"F0.wireOp",EDGE,"E1.bottom")])],"isStart":false});
            fillet(context, id + "F16", {"entities" : qUnion([Q0]), "radius" : 2 * mm, "tangentPropagation" : true, "allowEdgeOverflow" : false});
        }
    });
